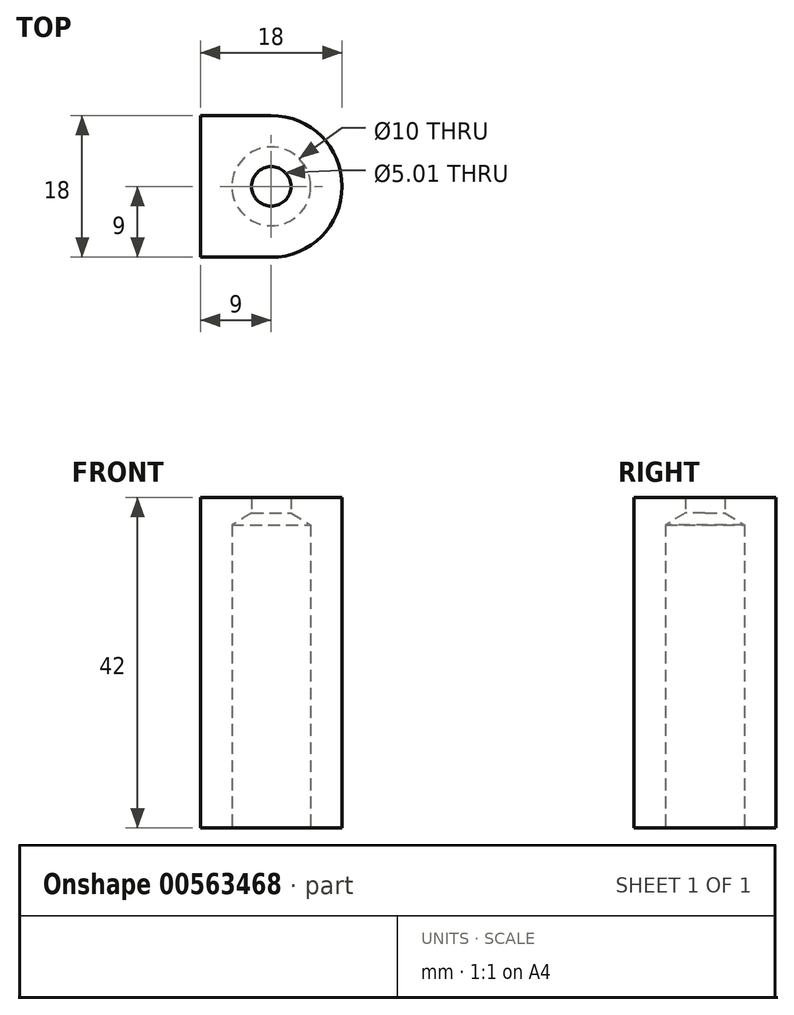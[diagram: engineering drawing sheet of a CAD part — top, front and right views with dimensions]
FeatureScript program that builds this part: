
annotation { "Feature Type Name" : "Feature", "Feature Type Description" : "" }
export const myFeature = defineFeature(function(context is Context, id is Id, definition is map)
    precondition{}
    {
        {
            var Q0;
            Q0=qCreatedBy(makeId("Top.planeOp"),FACE);
            var sketch = newSketch(context, id + "F0", { "sketchPlane" : qUnion([Q0])});
            skCircle(sketch, "E0", {"center": v(0, 0) * mm, "radius": 5 * mm});
            skCircle(sketch, "E1", {"center": v(0, 0) * mm, "radius": 9 * mm});
            skLineSegment(sketch, "E2.bottom", {"start": v(0, 9) * mm, "end": v(-9, 9) * mm});
            skLineSegment(sketch, "E2.top", {"start": v(0, -9) * mm, "end": v(-9, -9) * mm});
            skLineSegment(sketch, "E2.left", {"start": v(0, 9) * mm, "end": v(0, -9) * mm});
            skLineSegment(sketch, "E2.right", {"start": v(-9, 9) * mm, "end": v(-9, -9) * mm});
            skSolve(sketch);
        }
        {
            var Q0;
            {var subQ0=sQuery(id+"F0.wireOp",EDGE,"E2.left");var subQ5=sQuery(id+"F0.wireOp",EDGE,"E0");var subQ6=makeQuery(id+"F0.imprint","INTERSECT",VERTEX,{"disambiguationData":[OD(0.0)],"derivedFrom":[subQ5,subQ0]});Q0=makeQuery(id+"F0.imprint","IMPRINT",FACE,{"disambiguationData":[TD([[makeQuery(id+"F0.imprint","IMPRINT",EDGE,{"disambiguationData":[TD([[subQ6,-1.0]])],"derivedFrom":subQ5}),-1.0]])]});}
            var Q1;
            {var subQ0=sQuery(id+"F0.wireOp",EDGE,"E2.bottom");Q1=makeQuery(id+"F0.imprint","IMPRINT",FACE,{"disambiguationData":[TD([[makeQuery(id+"F0.imprint","IMPRINT",EDGE,{"derivedFrom":subQ0}),1.0]])]});}
            var Q2;
            {var subQ0=sQuery(id+"F0.wireOp",EDGE,"E2.top");Q2=makeQuery(id+"F0.imprint","IMPRINT",FACE,{"disambiguationData":[TD([[makeQuery(id+"F0.imprint","IMPRINT",EDGE,{"derivedFrom":subQ0}),-1.0]])]});}
            var Q3;
            {var subQ0=sQuery(id+"F0.wireOp",EDGE,"E2.left");var subQ1=sQuery(id+"F0.wireOp",EDGE,"E0");var subQ2=makeQuery(id+"F0.imprint","INTERSECT",VERTEX,{"disambiguationData":[OD(0.0)],"derivedFrom":[subQ1,subQ0]});Q3=makeQuery(id+"F0.imprint","IMPRINT",FACE,{"disambiguationData":[TD([[makeQuery(id+"F0.imprint","IMPRINT",EDGE,{"disambiguationData":[TD([[subQ2,1.0]])],"derivedFrom":subQ1}),-1.0]])]});}
            var Q4;
            {var subQ0=sQuery(id+"F0.wireOp",EDGE,"E2.left");var subQ1=sQuery(id+"F0.wireOp",EDGE,"E0");var subQ2=makeQuery(id+"F0.imprint","INTERSECT",VERTEX,{"disambiguationData":[OD(0.0)],"derivedFrom":[subQ1,subQ0]});Q4=makeQuery(id+"F0.imprint","IMPRINT",FACE,{"disambiguationData":[TD([[makeQuery(id+"F0.imprint","IMPRINT",EDGE,{"disambiguationData":[TD([[subQ2,-1.0]])],"derivedFrom":subQ1}),1.0]])]});}
            var Q5;
            {var subQ0=sQuery(id+"F0.wireOp",EDGE,"E2.left");var subQ1=sQuery(id+"F0.wireOp",EDGE,"E0");var subQ2=makeQuery(id+"F0.imprint","INTERSECT",VERTEX,{"disambiguationData":[OD(0.0)],"derivedFrom":[subQ1,subQ0]});Q5=makeQuery(id+"F0.imprint","IMPRINT",FACE,{"disambiguationData":[TD([[makeQuery(id+"F0.imprint","IMPRINT",EDGE,{"disambiguationData":[TD([[subQ2,1.0]])],"derivedFrom":subQ1}),1.0]])]});}
            extrude(context, id + "F1", {"entities" : qUnion([Q0, Q1, Q2, Q3, Q4, Q5]), "depth" : 40 * mm, "offsetDistance" : 25 * mm});
        }
        {
            var Q0;
            Q0=makeQuery(id+"F1.opExtrude","CAP_FACE",FACE,{"disambiguationData":[OSD([sQuery(id+"F0.wireOp",EDGE,"E1"),sQuery(id+"F0.wireOp",EDGE,"E2.bottom"),sQuery(id+"F0.wireOp",EDGE,"E2.top"),sQuery(id+"F0.wireOp",EDGE,"E2.right")])],"isStart":true});
            var sketch = newSketch(context, id + "F2", { "sketchPlane" : qUnion([Q0])});
            skPoint(sketch, "E3", {"position": v(0, 0) * mm});
            skSolve(sketch);
        }
        {
            var Q0;
            Q0=sQuery(id+"F2.wireOp",VERTEX,"E3");
            var Q1;
            Q1=makeQuery(id+"F1.opExtrude","SWEPT_BODY",BODY,{"disambiguationData":[OSD([sQuery(id+"F0.wireOp",EDGE,"E1"),sQuery(id+"F0.wireOp",EDGE,"E2.bottom"),sQuery(id+"F0.wireOp",EDGE,"E2.top"),sQuery(id+"F0.wireOp",EDGE,"E2.right")])]});
            hole(context, id + "F3", {"style" : HoleStyle.SIMPLE, "endStyle" : HoleEndStyle.BLIND, "holeDiameter" : 10 * mm, "holeDepth" : 38.5 * mm, "isTappedThrough" : true, "tappedDepth" : 12 * mm, "tapClearance" : 3, "locations" : qUnion([Q0]), "scope" : qUnion([Q1])});
        }
        {
            var Q0;
            Q0=makeQuery(id+"F1.opExtrude","CAP_FACE",FACE,{"disambiguationData":[OSD([sQuery(id+"F0.wireOp",EDGE,"E1"),sQuery(id+"F0.wireOp",EDGE,"E2.bottom"),sQuery(id+"F0.wireOp",EDGE,"E2.top"),sQuery(id+"F0.wireOp",EDGE,"E2.right")])],"isStart":false});
            extrude(context, id + "F4", {"entities" : qUnion([Q0]), "operationType" : NewBodyOperationType.ADD, "depth" : 2 * mm, "offsetDistance" : 25 * mm});
        }
    });
